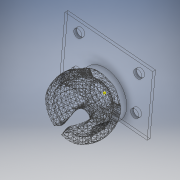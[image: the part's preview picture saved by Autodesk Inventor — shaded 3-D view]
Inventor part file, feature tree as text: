
AUTODESK INVENTOR PART (.ipt)
format: ipt  version: 2017 (Build 210142000, 142)  size: 2,589,184 bytes
history: native  units: in
note: dims shown in document units (in); Inventor stores cm internally (conversion verified against a paired STEP export)
features: sketch x8, extrude x7, projected_geometry x5, other x2, draft x1
ambient origin geometry x8: Origin, YZ Plane, XZ Plane, XY Plane, X Axis, Y Axis, Z Axis, Center Point
bodies: Solid1 (feature_tree)
feature tree (23):
  other  "ballSocket"
  other  "MeshFeature1"
  extrude  "Extrusion1"  Depth=0.4528in
  extrude  "Extrusion2"  TaperAngle=0.0deg  [1 undecoded]
  extrude  "Extrusion3"  TaperAngle=0.0deg  [1 undecoded]
  draft  "FaceDraft1"
  extrude  "Extrusion4"  TaperAngle=90.0deg  [1 undecoded]
  extrude  "Extrusion6"  Depth=0.1969in
  sketch  "Sketch7"  dims[d11=0.1969in d13=0.0787in]
  extrude  "Extrusion7"  Depth=0.0787in
  extrude  "Extrusion8"  Depth=0.0394in
  sketch  "Sketch1"  dims[d0=0.4528in d1=0.0in d2=0.2677in]
  sketch  "Sketch2"  dims[d3=0.3707in d4=0.0in]
  sketch  "Sketch3"  dims[d5=0.113in d6=0.0in]
  sketch  "Sketch4"  dims[d7=0.4079in d8=90.0deg]
  projected_geometry  "Projected Loop2"
  projected_geometry  "Projected Loop3"
  projected_geometry  "Projected Loop4"
  projected_geometry  "Projected Loop5"
  sketch  "Sketch6"  dims[d9=0.113in d10=0.1969in]
  sketch  "Sketch8"  dims[d14=0.0394in d15=0.0in]
  sketch  "Sketch9"  dims[d16=0.2677in d17=0.3569in d18=0.0in d19=0.113in d20=0.0in d22=0.113in d23=0.1969in d24=0.1969in d25=0.0787in d26=0.1575in d27=0.0in d28=0.1374in d29=0.1575in d30=0.0in d33=0.8268in d35=0.4921in d36=0.3937in d37=0.0in d38=0.0394in d39=0.0in d40=0.0492in d41=0.0in]
  projected_geometry  "Projected Loop7"
note: 3 required parameter values undecoded (feature->parameter linkage not recoverable at this tier; creation-order binding heuristic only, values carry confidence <= 0.55)
